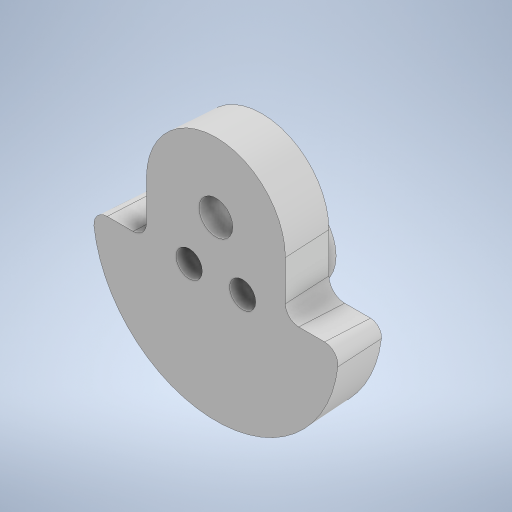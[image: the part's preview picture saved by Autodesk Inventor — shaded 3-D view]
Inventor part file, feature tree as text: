
AUTODESK INVENTOR PART (.ipt)
format: ipt  version: 2023 (Build 270158000, 158)  size: 498,688 bytes
history: native  units: in
note: dims shown in document units (in); Inventor stores cm internally (conversion verified against a paired STEP export)
features: extrude x5, draft x2, sketch x1, fillet x1
ambient origin geometry x8: Origin, YZ Plane, XZ Plane, XY Plane, X Axis, Y Axis, Z Axis, Center Point
bodies: Body1 (feature_tree)
feature tree (9):
  sketch  "Sketch1"  dims[d3=0.866in d15=0.75in d20=0.316in d37=0.75in d44=0.125in d52=0.245in d57=0.74in d58=0.75in d59=0.0in d60=0.32in d61=0.0in d62=1.5in d63=0.0in d64=1.5in d65=0.0in d66=0.375in d67=0.0in d68=0.125in d70=0.135in d71=0.0206in d72=0.0412in d73=1.15in]
  extrude  "Extrusion9"  Depth=0.125in
  extrude  "Extrusion10"  Depth=0.125in
  extrude  "Extrusion11"  Depth=0.125in
  extrude  "Extrusion12"  Depth=0.125in
  extrude  "Extrusion13"  Depth=0.125in
  fillet  "Fillet2"  Radius=0.75in
  draft  "FaceDraft1"
  draft  "FaceDraft2"
